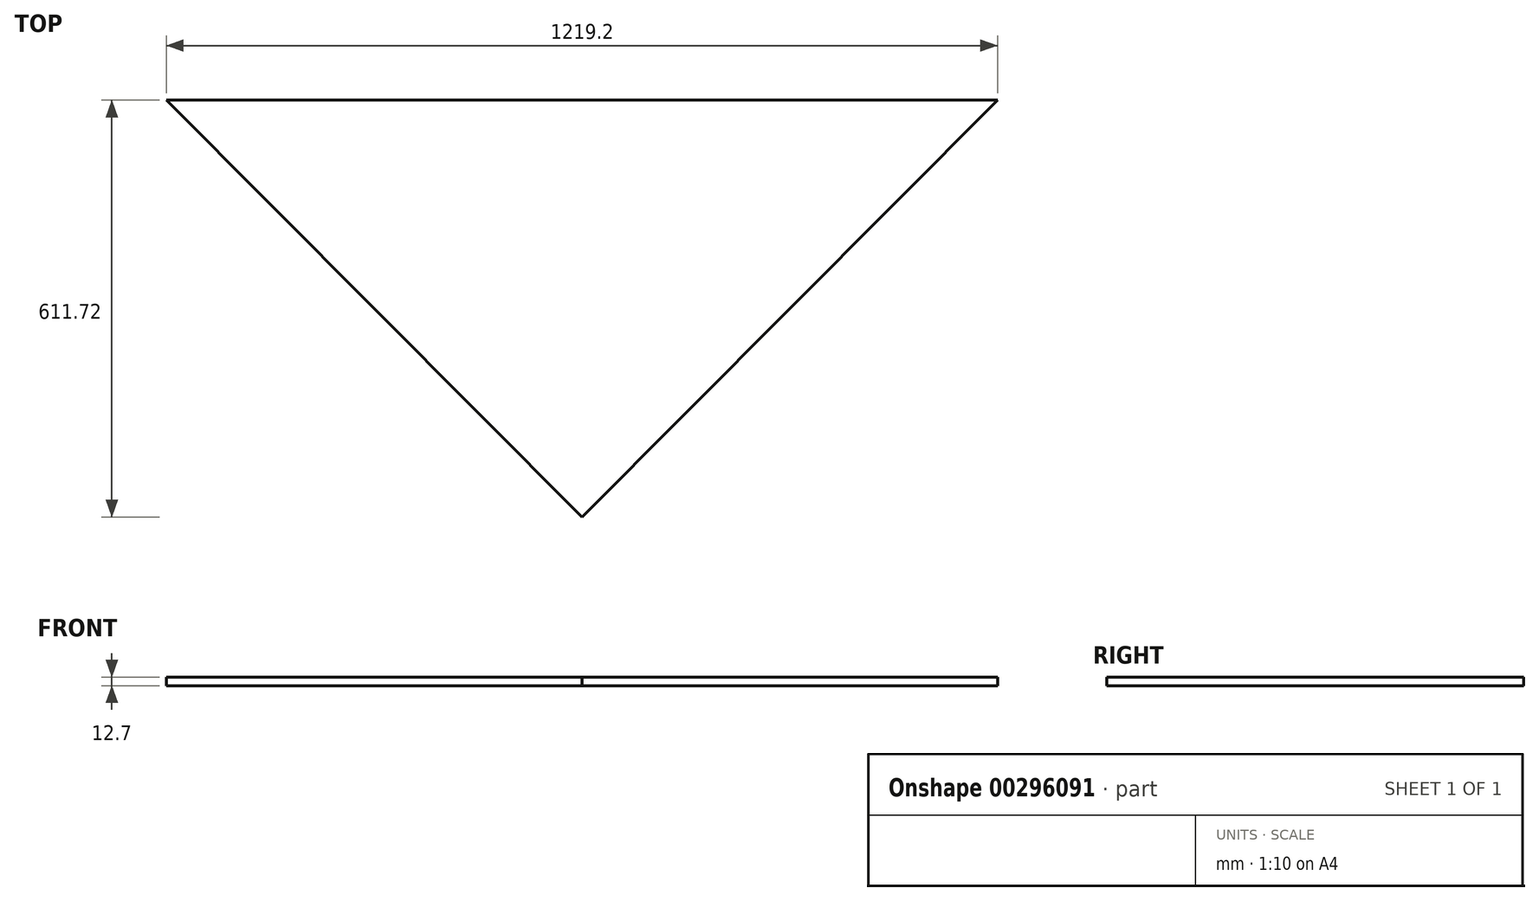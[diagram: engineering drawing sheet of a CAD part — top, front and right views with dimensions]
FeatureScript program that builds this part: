
annotation { "Feature Type Name" : "Feature", "Feature Type Description" : "" }
export const myFeature = defineFeature(function(context is Context, id is Id, definition is map)
    precondition{}
    {
        {
            var Q0;
            Q0=qCreatedBy(makeId("Top.planeOp"),FACE);
            var sketch = newSketch(context, id + "F0", { "sketchPlane" : qUnion([Q0])});
            skLineSegment(sketch, "E0", {"start": v(-609.6, 305.86) * mm, "end": v(609.6, 305.86) * mm});
            skLineSegment(sketch, "E1", {"start": v(609.6, 305.86) * mm, "end": v(0, -305.86) * mm});
            skLineSegment(sketch, "E2", {"start": v(0, -305.86) * mm, "end": v(-609.6, 305.86) * mm});
            skPoint(sketch, "E3", {"position": v(0, 305.86) * mm});
            skSolve(sketch);
        }
        {
            var Q0;
            Q0=makeQuery(id+"F0.imprint","IMPRINT",FACE,{"disambiguationData":[TD([[makeQuery(id+"F0.imprint","IMPRINT",EDGE,{"derivedFrom":sQuery(id+"F0.wireOp",EDGE,"E0")}),-1.0]])]});
            extrude(context, id + "F1", {"entities" : qUnion([Q0]), "depth" : 12.7 * mm});
        }
    });
